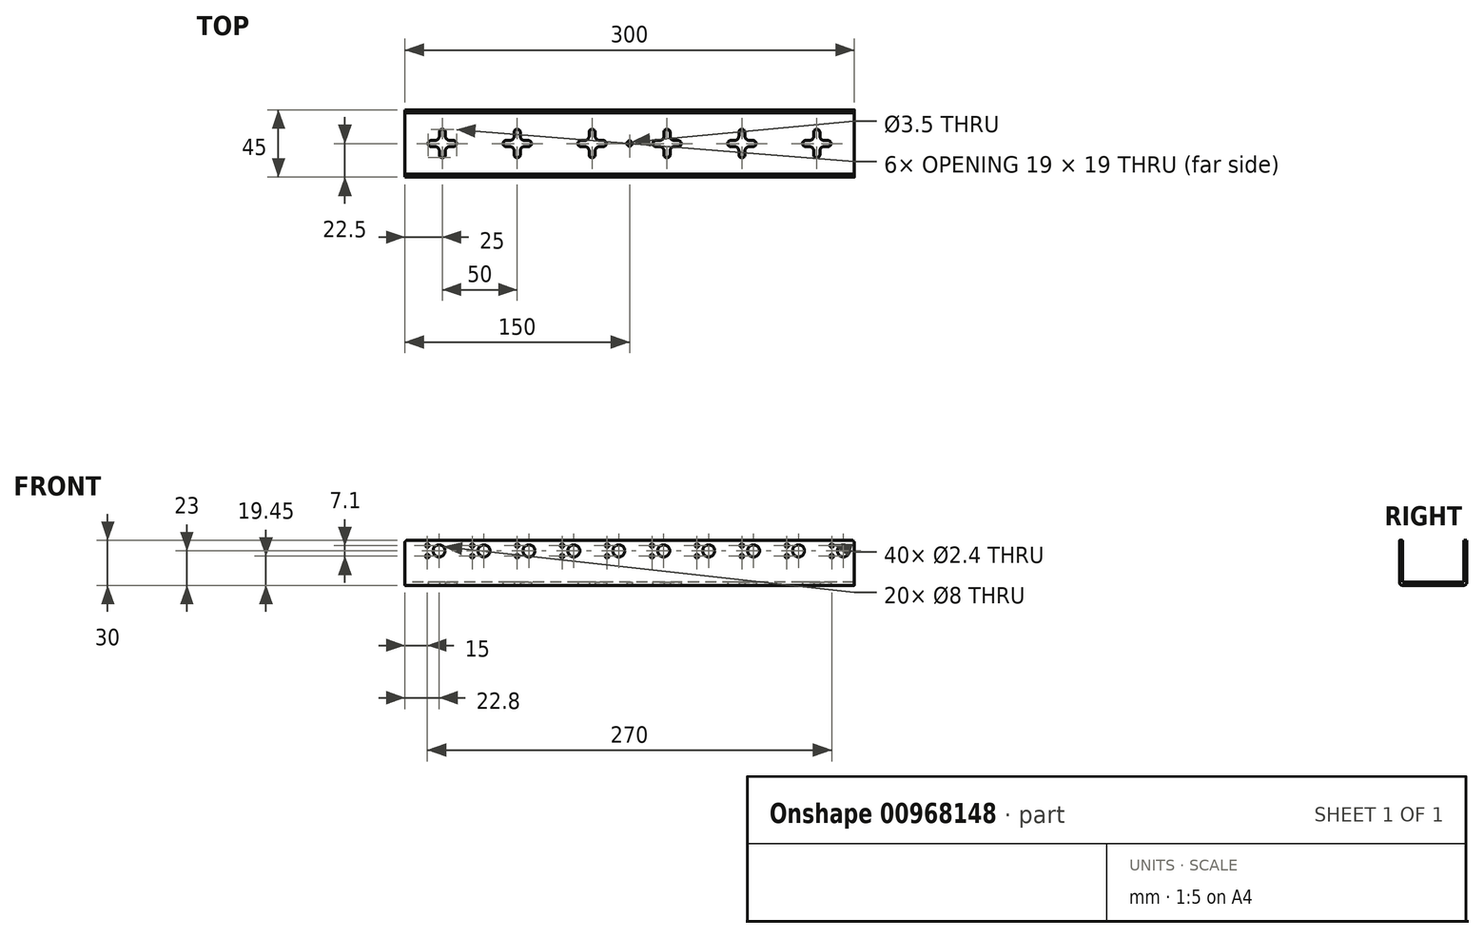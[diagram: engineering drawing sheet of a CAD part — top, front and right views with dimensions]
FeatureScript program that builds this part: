
annotation { "Feature Type Name" : "Feature", "Feature Type Description" : "" }
export const myFeature = defineFeature(function(context is Context, id is Id, definition is map)
    precondition{}
    {
        {
            var Q0;
            Q0=qCreatedBy(makeId("Right.planeOp"),FACE);
            var sketch = newSketch(context, id + "F0", { "sketchPlane" : qUnion([Q0])});
            skLineSegment(sketch, "E0", {"start": v(0, 30) * mm, "end": v(0, 0) * mm});
            skLineSegment(sketch, "E1", {"start": v(0, 0) * mm, "end": v(45, 0) * mm});
            skLineSegment(sketch, "E2", {"start": v(45, 0) * mm, "end": v(45, 30) * mm});
            skLineSegment(sketch, "E3.0", {"start": v(2, 30) * mm, "end": v(2, 0) * mm});
            skLineSegment(sketch, "E4.0", {"start": v(43, 0) * mm, "end": v(43, 30) * mm});
            skLineSegment(sketch, "E5.0", {"start": v(0, 2) * mm, "end": v(60, 2) * mm});
            skLineSegment(sketch, "E6", {"start": v(0, 30) * mm, "end": v(45, 30) * mm});
            skSolve(sketch);
        }
        {
            var Q0;
            {var subQ0=sQuery(id+"F0.wireOp",EDGE,"E6");var subQ1=sQuery(id+"F0.wireOp",EDGE,"E0");var subQ2=makeQuery(id+"F0.imprint","INTERSECT",VERTEX,{"derivedFrom":[subQ1,subQ0]});Q0=makeQuery(id+"F0.imprint","IMPRINT",FACE,{"disambiguationData":[TD([[makeQuery(id+"F0.imprint","IMPRINT",EDGE,{"disambiguationData":[TD([[subQ2,-1.0]])],"derivedFrom":subQ1}),1.0]])]});}
            var Q1;
            {var subQ0=sQuery(id+"F0.wireOp",EDGE,"E1");var subQ1=sQuery(id+"F0.wireOp",EDGE,"E0");var subQ2=makeQuery(id+"F0.imprint","INTERSECT",VERTEX,{"derivedFrom":[subQ1,subQ0]});Q1=makeQuery(id+"F0.imprint","IMPRINT",FACE,{"disambiguationData":[TD([[makeQuery(id+"F0.imprint","IMPRINT",EDGE,{"disambiguationData":[TD([[subQ2,1.0]])],"derivedFrom":subQ1}),1.0]])]});}
            var Q2;
            {var subQ0=sQuery(id+"F0.wireOp",EDGE,"E3.0");var subQ1=sQuery(id+"F0.wireOp",EDGE,"E1");var subQ2=makeQuery(id+"F0.imprint","INTERSECT",VERTEX,{"derivedFrom":[subQ1,subQ0]});Q2=makeQuery(id+"F0.imprint","IMPRINT",FACE,{"disambiguationData":[TD([[makeQuery(id+"F0.imprint","IMPRINT",EDGE,{"disambiguationData":[TD([[subQ2,-1.0]])],"derivedFrom":subQ1}),1.0]])]});}
            var Q3;
            {var subQ0=sQuery(id+"F0.wireOp",EDGE,"E2");var subQ1=sQuery(id+"F0.wireOp",EDGE,"E1");var subQ2=makeQuery(id+"F0.imprint","INTERSECT",VERTEX,{"derivedFrom":[subQ1,subQ0]});Q3=makeQuery(id+"F0.imprint","IMPRINT",FACE,{"disambiguationData":[TD([[makeQuery(id+"F0.imprint","IMPRINT",EDGE,{"disambiguationData":[TD([[subQ2,1.0]])],"derivedFrom":subQ1}),1.0]])]});}
            var Q4;
            {var subQ0=sQuery(id+"F0.wireOp",EDGE,"E6");var subQ1=sQuery(id+"F0.wireOp",EDGE,"E2");var subQ2=makeQuery(id+"F0.imprint","INTERSECT",VERTEX,{"derivedFrom":[subQ1,subQ0]});Q4=makeQuery(id+"F0.imprint","IMPRINT",FACE,{"disambiguationData":[TD([[makeQuery(id+"F0.imprint","IMPRINT",EDGE,{"disambiguationData":[TD([[subQ2,1.0]])],"derivedFrom":subQ1}),1.0]])]});}
            extrude(context, id + "F1", {"entities" : qUnion([Q0, Q1, Q2, Q3, Q4]), "endBound" : BoundingType.SYMMETRIC, "depth" : 300 * mm, "offsetDistance" : 25 * mm});
        }
        {
            var Q0;
            Q0=makeQuery(id+"F1.opExtrude","SWEPT_FACE",FACE,{"disambiguationData":[OSD([sQuery(id+"F0.wireOp",EDGE,"E0")])]});
            var sketch = newSketch(context, id + "F2", { "sketchPlane" : qUnion([Q0])});
            skCircle(sketch, "E7", {"center": v(-135, 26.55) * mm, "radius": 1.2 * mm});
            skCircle(sketch, "E8", {"center": v(-135, 19.45) * mm, "radius": 1.2 * mm});
            skCircle(sketch, "E9", {"center": v(-127.2, 23) * mm, "radius": 4 * mm});
            skCircle(sketch, "E10", {"center": v(-105, 26.55) * mm, "radius": 1.2 * mm});
            skCircle(sketch, "E11", {"center": v(-105, 19.45) * mm, "radius": 1.2 * mm});
            skCircle(sketch, "E12", {"center": v(-97.2, 23) * mm, "radius": 4 * mm});
            skCircle(sketch, "E13.1.0.0", {"center": v(-75, 19.45) * mm, "radius": 1.2 * mm});
            skCircle(sketch, "E13.1.0.1", {"center": v(-67.2, 23) * mm, "radius": 4 * mm});
            skCircle(sketch, "E13.1.0.2", {"center": v(-75, 26.55) * mm, "radius": 1.2 * mm});
            skCircle(sketch, "E13.2.0.0", {"center": v(-45, 19.45) * mm, "radius": 1.2 * mm});
            skCircle(sketch, "E13.2.0.1", {"center": v(-37.2, 23) * mm, "radius": 4 * mm});
            skCircle(sketch, "E13.2.0.2", {"center": v(-45, 26.55) * mm, "radius": 1.2 * mm});
            skCircle(sketch, "E13.3.0.0", {"center": v(-15, 19.45) * mm, "radius": 1.2 * mm});
            skCircle(sketch, "E13.3.0.1", {"center": v(-7.2, 23) * mm, "radius": 4 * mm});
            skCircle(sketch, "E13.3.0.2", {"center": v(-15, 26.55) * mm, "radius": 1.2 * mm});
            skCircle(sketch, "E13.4.0.0", {"center": v(15, 19.45) * mm, "radius": 1.2 * mm});
            skCircle(sketch, "E13.4.0.1", {"center": v(22.8, 23) * mm, "radius": 4 * mm});
            skCircle(sketch, "E13.4.0.2", {"center": v(15, 26.55) * mm, "radius": 1.2 * mm});
            skCircle(sketch, "E13.5.0.0", {"center": v(45, 19.45) * mm, "radius": 1.2 * mm});
            skCircle(sketch, "E13.5.0.1", {"center": v(52.8, 23) * mm, "radius": 4 * mm});
            skCircle(sketch, "E13.5.0.2", {"center": v(45, 26.55) * mm, "radius": 1.2 * mm});
            skCircle(sketch, "E13.6.0.0", {"center": v(75, 19.45) * mm, "radius": 1.2 * mm});
            skCircle(sketch, "E13.6.0.1", {"center": v(82.8, 23) * mm, "radius": 4 * mm});
            skCircle(sketch, "E13.6.0.2", {"center": v(75, 26.55) * mm, "radius": 1.2 * mm});
            skCircle(sketch, "E13.7.0.0", {"center": v(105, 19.45) * mm, "radius": 1.2 * mm});
            skCircle(sketch, "E13.7.0.1", {"center": v(112.8, 23) * mm, "radius": 4 * mm});
            skCircle(sketch, "E13.7.0.2", {"center": v(105, 26.55) * mm, "radius": 1.2 * mm});
            skCircle(sketch, "E13.8.0.0", {"center": v(135, 19.45) * mm, "radius": 1.2 * mm});
            skCircle(sketch, "E13.8.0.1", {"center": v(142.8, 23) * mm, "radius": 4 * mm});
            skCircle(sketch, "E13.8.0.2", {"center": v(135, 26.55) * mm, "radius": 1.2 * mm});
            skLineSegment(sketch, "E13.direction1", {"start": v(-105, 19.45) * mm, "end": v(-75, 19.45) * mm, "construction": true});
            skSolve(sketch);
        }
        {
            var Q0;
            Q0=makeQuery(id+"F2.imprint","IMPRINT",FACE,{"disambiguationData":[TD([[makeQuery(id+"F2.imprint","IMPRINT",EDGE,{"derivedFrom":sQuery(id+"F2.wireOp",EDGE,"E7")}),1.0]])]});
            var Q1;
            Q1=makeQuery(id+"F2.imprint","IMPRINT",FACE,{"disambiguationData":[TD([[makeQuery(id+"F2.imprint","IMPRINT",EDGE,{"derivedFrom":sQuery(id+"F2.wireOp",EDGE,"E8")}),1.0]])]});
            var Q2;
            Q2=makeQuery(id+"F2.imprint","IMPRINT",FACE,{"disambiguationData":[TD([[makeQuery(id+"F2.imprint","IMPRINT",EDGE,{"derivedFrom":sQuery(id+"F2.wireOp",EDGE,"E10")}),1.0]])]});
            var Q3;
            Q3=makeQuery(id+"F2.imprint","IMPRINT",FACE,{"disambiguationData":[TD([[makeQuery(id+"F2.imprint","IMPRINT",EDGE,{"derivedFrom":sQuery(id+"F2.wireOp",EDGE,"E11")}),1.0]])]});
            var Q4;
            Q4=makeQuery(id+"F2.imprint","IMPRINT",FACE,{"disambiguationData":[TD([[makeQuery(id+"F2.imprint","IMPRINT",EDGE,{"derivedFrom":sQuery(id+"F2.wireOp",EDGE,"E12")}),1.0]])]});
            var Q5;
            Q5=makeQuery(id+"F2.imprint","IMPRINT",FACE,{"disambiguationData":[TD([[makeQuery(id+"F2.imprint","IMPRINT",EDGE,{"derivedFrom":sQuery(id+"F2.wireOp",EDGE,"E13.1.0.1")}),1.0]])]});
            var Q6;
            Q6=makeQuery(id+"F2.imprint","IMPRINT",FACE,{"disambiguationData":[TD([[makeQuery(id+"F2.imprint","IMPRINT",EDGE,{"derivedFrom":sQuery(id+"F2.wireOp",EDGE,"E13.1.0.2")}),1.0]])]});
            var Q7;
            Q7=makeQuery(id+"F2.imprint","IMPRINT",FACE,{"disambiguationData":[TD([[makeQuery(id+"F2.imprint","IMPRINT",EDGE,{"derivedFrom":sQuery(id+"F2.wireOp",EDGE,"E13.1.0.0")}),1.0]])]});
            var Q8;
            Q8=makeQuery(id+"F2.imprint","IMPRINT",FACE,{"disambiguationData":[TD([[makeQuery(id+"F2.imprint","IMPRINT",EDGE,{"derivedFrom":sQuery(id+"F2.wireOp",EDGE,"E13.2.0.0")}),1.0]])]});
            var Q9;
            Q9=makeQuery(id+"F2.imprint","IMPRINT",FACE,{"disambiguationData":[TD([[makeQuery(id+"F2.imprint","IMPRINT",EDGE,{"derivedFrom":sQuery(id+"F2.wireOp",EDGE,"E13.3.0.1")}),1.0]])]});
            var Q10;
            Q10=makeQuery(id+"F2.imprint","IMPRINT",FACE,{"disambiguationData":[TD([[makeQuery(id+"F2.imprint","IMPRINT",EDGE,{"derivedFrom":sQuery(id+"F2.wireOp",EDGE,"E13.3.0.2")}),1.0]])]});
            var Q11;
            Q11=makeQuery(id+"F2.imprint","IMPRINT",FACE,{"disambiguationData":[TD([[makeQuery(id+"F2.imprint","IMPRINT",EDGE,{"derivedFrom":sQuery(id+"F2.wireOp",EDGE,"E9")}),1.0]])]});
            var Q12;
            Q12=makeQuery(id+"F2.imprint","IMPRINT",FACE,{"disambiguationData":[TD([[makeQuery(id+"F2.imprint","IMPRINT",EDGE,{"derivedFrom":sQuery(id+"F2.wireOp",EDGE,"E13.2.0.1")}),1.0]])]});
            var Q13;
            Q13=makeQuery(id+"F2.imprint","IMPRINT",FACE,{"disambiguationData":[TD([[makeQuery(id+"F2.imprint","IMPRINT",EDGE,{"derivedFrom":sQuery(id+"F2.wireOp",EDGE,"E13.2.0.2")}),1.0]])]});
            var Q14;
            Q14=makeQuery(id+"F2.imprint","IMPRINT",FACE,{"disambiguationData":[TD([[makeQuery(id+"F2.imprint","IMPRINT",EDGE,{"derivedFrom":sQuery(id+"F2.wireOp",EDGE,"E13.3.0.0")}),1.0]])]});
            var Q15;
            Q15=makeQuery(id+"F2.imprint","IMPRINT",FACE,{"disambiguationData":[TD([[makeQuery(id+"F2.imprint","IMPRINT",EDGE,{"derivedFrom":sQuery(id+"F2.wireOp",EDGE,"E13.4.0.1")}),1.0]])]});
            var Q16;
            Q16=makeQuery(id+"F2.imprint","IMPRINT",FACE,{"disambiguationData":[TD([[makeQuery(id+"F2.imprint","IMPRINT",EDGE,{"derivedFrom":sQuery(id+"F2.wireOp",EDGE,"E13.4.0.2")}),1.0]])]});
            var Q17;
            Q17=makeQuery(id+"F2.imprint","IMPRINT",FACE,{"disambiguationData":[TD([[makeQuery(id+"F2.imprint","IMPRINT",EDGE,{"derivedFrom":sQuery(id+"F2.wireOp",EDGE,"E13.4.0.0")}),1.0]])]});
            var Q18;
            Q18=makeQuery(id+"F2.imprint","IMPRINT",FACE,{"disambiguationData":[TD([[makeQuery(id+"F2.imprint","IMPRINT",EDGE,{"derivedFrom":sQuery(id+"F2.wireOp",EDGE,"E13.5.0.1")}),1.0]])]});
            var Q19;
            Q19=makeQuery(id+"F2.imprint","IMPRINT",FACE,{"disambiguationData":[TD([[makeQuery(id+"F2.imprint","IMPRINT",EDGE,{"derivedFrom":sQuery(id+"F2.wireOp",EDGE,"E13.5.0.2")}),1.0]])]});
            var Q20;
            Q20=makeQuery(id+"F2.imprint","IMPRINT",FACE,{"disambiguationData":[TD([[makeQuery(id+"F2.imprint","IMPRINT",EDGE,{"derivedFrom":sQuery(id+"F2.wireOp",EDGE,"E13.5.0.0")}),1.0]])]});
            var Q21;
            Q21=makeQuery(id+"F2.imprint","IMPRINT",FACE,{"disambiguationData":[TD([[makeQuery(id+"F2.imprint","IMPRINT",EDGE,{"derivedFrom":sQuery(id+"F2.wireOp",EDGE,"E13.6.0.1")}),1.0]])]});
            var Q22;
            Q22=makeQuery(id+"F2.imprint","IMPRINT",FACE,{"disambiguationData":[TD([[makeQuery(id+"F2.imprint","IMPRINT",EDGE,{"derivedFrom":sQuery(id+"F2.wireOp",EDGE,"E13.6.0.0")}),1.0]])]});
            var Q23;
            Q23=makeQuery(id+"F2.imprint","IMPRINT",FACE,{"disambiguationData":[TD([[makeQuery(id+"F2.imprint","IMPRINT",EDGE,{"derivedFrom":sQuery(id+"F2.wireOp",EDGE,"E13.6.0.2")}),1.0]])]});
            var Q24;
            Q24=makeQuery(id+"F2.imprint","IMPRINT",FACE,{"disambiguationData":[TD([[makeQuery(id+"F2.imprint","IMPRINT",EDGE,{"derivedFrom":sQuery(id+"F2.wireOp",EDGE,"E13.7.0.1")}),1.0]])]});
            var Q25;
            Q25=makeQuery(id+"F2.imprint","IMPRINT",FACE,{"disambiguationData":[TD([[makeQuery(id+"F2.imprint","IMPRINT",EDGE,{"derivedFrom":sQuery(id+"F2.wireOp",EDGE,"E13.7.0.2")}),1.0]])]});
            var Q26;
            Q26=makeQuery(id+"F2.imprint","IMPRINT",FACE,{"disambiguationData":[TD([[makeQuery(id+"F2.imprint","IMPRINT",EDGE,{"derivedFrom":sQuery(id+"F2.wireOp",EDGE,"E13.7.0.0")}),1.0]])]});
            var Q27;
            Q27=makeQuery(id+"F2.imprint","IMPRINT",FACE,{"disambiguationData":[TD([[makeQuery(id+"F2.imprint","IMPRINT",EDGE,{"derivedFrom":sQuery(id+"F2.wireOp",EDGE,"E13.8.0.1")}),1.0]])]});
            var Q28;
            Q28=makeQuery(id+"F2.imprint","IMPRINT",FACE,{"disambiguationData":[TD([[makeQuery(id+"F2.imprint","IMPRINT",EDGE,{"derivedFrom":sQuery(id+"F2.wireOp",EDGE,"E13.8.0.2")}),1.0]])]});
            var Q29;
            Q29=makeQuery(id+"F2.imprint","IMPRINT",FACE,{"disambiguationData":[TD([[makeQuery(id+"F2.imprint","IMPRINT",EDGE,{"derivedFrom":sQuery(id+"F2.wireOp",EDGE,"E13.8.0.0")}),1.0]])]});
            extrude(context, id + "F3", {"entities" : qUnion([Q0, Q1, Q2, Q3, Q4, Q5, Q6, Q7, Q8, Q9, Q10, Q11, Q12, Q13, Q14, Q15, Q16, Q17, Q18, Q19, Q20, Q21, Q22, Q23, Q24, Q25, Q26, Q27, Q28, Q29]), "operationType" : NewBodyOperationType.REMOVE, "endBound" : BoundingType.THROUGH_ALL, "oppositeDirection" : true, "depth" : 25 * mm, "offsetDistance" : 25 * mm});
        }
        {
            var Q0;
            {var subQ0=sQuery(id+"F0.wireOp",EDGE,"E6");Q0=makeQuery(id+"F1.opExtrude","CAP_EDGE",EDGE,{"disambiguationData":[OSD([subQ0]),TDD([makeQuery(id+"F0.imprint","IMPRINT",EDGE,{"disambiguationData":[TD([[makeQuery(id+"F0.imprint","INTERSECT",VERTEX,{"derivedFrom":[sQuery(id+"F0.wireOp",EDGE,"E2"),subQ0]}),1.0]])],"derivedFrom":subQ0})])],"isStart":true});}
            var Q1;
            {var subQ0=sQuery(id+"F0.wireOp",EDGE,"E6");Q1=makeQuery(id+"F1.opExtrude","CAP_EDGE",EDGE,{"disambiguationData":[OSD([subQ0]),TDD([makeQuery(id+"F0.imprint","IMPRINT",EDGE,{"disambiguationData":[TD([[makeQuery(id+"F0.imprint","INTERSECT",VERTEX,{"derivedFrom":[sQuery(id+"F0.wireOp",EDGE,"E2"),subQ0]}),1.0]])],"derivedFrom":subQ0})])],"isStart":false});}
            var Q2;
            {var subQ0=sQuery(id+"F0.wireOp",EDGE,"E6");Q2=makeQuery(id+"F1.opExtrude","CAP_EDGE",EDGE,{"disambiguationData":[OSD([subQ0]),TDD([makeQuery(id+"F0.imprint","IMPRINT",EDGE,{"disambiguationData":[TD([[makeQuery(id+"F0.imprint","INTERSECT",VERTEX,{"derivedFrom":[sQuery(id+"F0.wireOp",EDGE,"E0"),subQ0]}),-1.0]])],"derivedFrom":subQ0})])],"isStart":false});}
            var Q3;
            {var subQ0=sQuery(id+"F0.wireOp",EDGE,"E6");Q3=makeQuery(id+"F1.opExtrude","CAP_EDGE",EDGE,{"disambiguationData":[OSD([subQ0]),TDD([makeQuery(id+"F0.imprint","IMPRINT",EDGE,{"disambiguationData":[TD([[makeQuery(id+"F0.imprint","INTERSECT",VERTEX,{"derivedFrom":[sQuery(id+"F0.wireOp",EDGE,"E0"),subQ0]}),-1.0]])],"derivedFrom":subQ0})])],"isStart":true});}
            fillet(context, id + "F4", {"entities" : qUnion([Q0, Q1, Q2, Q3]), "radius" : 1.5 * mm, "tangentPropagation" : true, "allowEdgeOverflow" : false});
        }
        {
            var Q0;
            Q0=makeQuery(id+"F1.opExtrude","SWEPT_EDGE",EDGE,{"disambiguationData":[OSD([sQuery(id+"F0.wireOp",EDGE,"E0"),sQuery(id+"F0.wireOp",EDGE,"E1")])]});
            var Q1;
            Q1=makeQuery(id+"F1.opExtrude","SWEPT_EDGE",EDGE,{"disambiguationData":[OSD([sQuery(id+"F0.wireOp",EDGE,"E1"),sQuery(id+"F0.wireOp",EDGE,"E2")])]});
            fillet(context, id + "F5", {"entities" : qUnion([Q0, Q1]), "radius" : 2 * mm, "tangentPropagation" : true, "allowEdgeOverflow" : false});
        }
        {
            var Q0;
            Q0=makeQuery(id+"F1.opExtrude","SWEPT_FACE",FACE,{"disambiguationData":[OSD([sQuery(id+"F0.wireOp",EDGE,"E1")])]});
            var sketch = newSketch(context, id + "F6", { "sketchPlane" : qUnion([Q0])});
            skCircle(sketch, "E14", {"center": v(0, -22.5) * mm, "radius": 1.75 * mm});
            skLineSegment(sketch, "E15", {"start": v(-25, -30) * mm, "end": v(-25, -15) * mm});
            skLineSegment(sketch, "E16", {"start": v(-17.5, -22.5) * mm, "end": v(-32.5, -22.5) * mm});
            skArc(sketch, "E17.0.startCap", {"start": v(-17.5, -20.5) * mm, "mid": v(-15.5, -22.5) * mm, "end": v(-17.5, -24.5) * mm});
            skArc(sketch, "E17.0.endCap", {"start": v(-32.5, -24.5) * mm, "mid": v(-34.5, -22.5) * mm, "end": v(-32.5, -20.5) * mm});
            skLineSegment(sketch, "E17.0.left", {"start": v(-17.5, -24.5) * mm, "end": v(-32.5, -24.5) * mm});
            skLineSegment(sketch, "E17.0.right", {"start": v(-17.5, -20.5) * mm, "end": v(-32.5, -20.5) * mm});
            skArc(sketch, "E17.1.startCap", {"start": v(-23, -30) * mm, "mid": v(-25, -32) * mm, "end": v(-27, -30) * mm});
            skArc(sketch, "E17.1.endCap", {"start": v(-27, -15) * mm, "mid": v(-25, -13) * mm, "end": v(-23, -15) * mm});
            skLineSegment(sketch, "E17.1.left", {"start": v(-27, -30) * mm, "end": v(-27, -15) * mm});
            skLineSegment(sketch, "E17.1.right", {"start": v(-23, -30) * mm, "end": v(-23, -15) * mm});
            skArc(sketch, "E18.1.0.0", {"start": v(-82.5, -24.5) * mm, "mid": v(-84.5, -22.5) * mm, "end": v(-82.5, -20.5) * mm});
            skArc(sketch, "E18.1.0.1", {"start": v(-77, -15) * mm, "mid": v(-75, -13) * mm, "end": v(-73, -15) * mm});
            skLineSegment(sketch, "E18.1.0.2", {"start": v(-73, -30) * mm, "end": v(-73, -15) * mm});
            skLineSegment(sketch, "E18.1.0.3", {"start": v(-67.5, -24.5) * mm, "end": v(-82.5, -24.5) * mm});
            skArc(sketch, "E18.1.0.4", {"start": v(-67.5, -20.5) * mm, "mid": v(-65.5, -22.5) * mm, "end": v(-67.5, -24.5) * mm});
            skLineSegment(sketch, "E18.1.0.5", {"start": v(-75, -30) * mm, "end": v(-75, -15) * mm});
            skArc(sketch, "E18.1.0.6", {"start": v(-73, -30) * mm, "mid": v(-75, -32) * mm, "end": v(-77, -30) * mm});
            skLineSegment(sketch, "E18.1.0.7", {"start": v(-67.5, -22.5) * mm, "end": v(-82.5, -22.5) * mm});
            skLineSegment(sketch, "E18.1.0.8", {"start": v(-77, -30) * mm, "end": v(-77, -15) * mm});
            skLineSegment(sketch, "E18.1.0.9", {"start": v(-67.5, -20.5) * mm, "end": v(-82.5, -20.5) * mm});
            skArc(sketch, "E18.2.0.0", {"start": v(-132.5, -24.5) * mm, "mid": v(-134.5, -22.5) * mm, "end": v(-132.5, -20.5) * mm});
            skArc(sketch, "E18.2.0.1", {"start": v(-127, -15) * mm, "mid": v(-125, -13) * mm, "end": v(-123, -15) * mm});
            skLineSegment(sketch, "E18.2.0.2", {"start": v(-123, -30) * mm, "end": v(-123, -15) * mm});
            skLineSegment(sketch, "E18.2.0.3", {"start": v(-117.5, -24.5) * mm, "end": v(-132.5, -24.5) * mm});
            skArc(sketch, "E18.2.0.4", {"start": v(-117.5, -20.5) * mm, "mid": v(-115.5, -22.5) * mm, "end": v(-117.5, -24.5) * mm});
            skLineSegment(sketch, "E18.2.0.5", {"start": v(-125, -30) * mm, "end": v(-125, -15) * mm});
            skArc(sketch, "E18.2.0.6", {"start": v(-123, -30) * mm, "mid": v(-125, -32) * mm, "end": v(-127, -30) * mm});
            skLineSegment(sketch, "E18.2.0.7", {"start": v(-117.5, -22.5) * mm, "end": v(-132.5, -22.5) * mm});
            skLineSegment(sketch, "E18.2.0.8", {"start": v(-127, -30) * mm, "end": v(-127, -15) * mm});
            skLineSegment(sketch, "E18.2.0.9", {"start": v(-117.5, -20.5) * mm, "end": v(-132.5, -20.5) * mm});
            skLineSegment(sketch, "E18.direction1", {"start": v(-27, -30) * mm, "end": v(-77, -30) * mm, "construction": true});
            skLineSegment(sketch, "E19.1.0.0", {"start": v(25, -30) * mm, "end": v(25, -15) * mm});
            skArc(sketch, "E19.1.0.1", {"start": v(32.5, -20.5) * mm, "mid": v(34.5, -22.5) * mm, "end": v(32.5, -24.5) * mm});
            skArc(sketch, "E19.1.0.2", {"start": v(17.5, -24.5) * mm, "mid": v(15.5, -22.5) * mm, "end": v(17.5, -20.5) * mm});
            skLineSegment(sketch, "E19.1.0.3", {"start": v(27, -30) * mm, "end": v(27, -15) * mm});
            skLineSegment(sketch, "E19.1.0.4", {"start": v(32.5, -24.5) * mm, "end": v(17.5, -24.5) * mm});
            skLineSegment(sketch, "E19.1.0.5", {"start": v(32.5, -22.5) * mm, "end": v(17.5, -22.5) * mm});
            skArc(sketch, "E19.1.0.6", {"start": v(27, -30) * mm, "mid": v(25, -32) * mm, "end": v(23, -30) * mm});
            skLineSegment(sketch, "E19.1.0.7", {"start": v(23, -30) * mm, "end": v(23, -15) * mm});
            skLineSegment(sketch, "E19.1.0.8", {"start": v(32.5, -20.5) * mm, "end": v(17.5, -20.5) * mm});
            skArc(sketch, "E19.1.0.9", {"start": v(23, -15) * mm, "mid": v(25, -13) * mm, "end": v(27, -15) * mm});
            skLineSegment(sketch, "E19.2.0.0", {"start": v(75, -30) * mm, "end": v(75, -15) * mm});
            skArc(sketch, "E19.2.0.1", {"start": v(82.5, -20.5) * mm, "mid": v(84.5, -22.5) * mm, "end": v(82.5, -24.5) * mm});
            skArc(sketch, "E19.2.0.2", {"start": v(67.5, -24.5) * mm, "mid": v(65.5, -22.5) * mm, "end": v(67.5, -20.5) * mm});
            skLineSegment(sketch, "E19.2.0.3", {"start": v(77, -30) * mm, "end": v(77, -15) * mm});
            skLineSegment(sketch, "E19.2.0.4", {"start": v(82.5, -24.5) * mm, "end": v(67.5, -24.5) * mm});
            skLineSegment(sketch, "E19.2.0.5", {"start": v(82.5, -22.5) * mm, "end": v(67.5, -22.5) * mm});
            skArc(sketch, "E19.2.0.6", {"start": v(77, -30) * mm, "mid": v(75, -32) * mm, "end": v(73, -30) * mm});
            skLineSegment(sketch, "E19.2.0.7", {"start": v(73, -30) * mm, "end": v(73, -15) * mm});
            skLineSegment(sketch, "E19.2.0.8", {"start": v(82.5, -20.5) * mm, "end": v(67.5, -20.5) * mm});
            skArc(sketch, "E19.2.0.9", {"start": v(73, -15) * mm, "mid": v(75, -13) * mm, "end": v(77, -15) * mm});
            skLineSegment(sketch, "E19.3.0.0", {"start": v(125, -30) * mm, "end": v(125, -15) * mm});
            skArc(sketch, "E19.3.0.1", {"start": v(132.5, -20.5) * mm, "mid": v(134.5, -22.5) * mm, "end": v(132.5, -24.5) * mm});
            skArc(sketch, "E19.3.0.2", {"start": v(117.5, -24.5) * mm, "mid": v(115.5, -22.5) * mm, "end": v(117.5, -20.5) * mm});
            skLineSegment(sketch, "E19.3.0.3", {"start": v(127, -30) * mm, "end": v(127, -15) * mm});
            skLineSegment(sketch, "E19.3.0.4", {"start": v(132.5, -24.5) * mm, "end": v(117.5, -24.5) * mm});
            skLineSegment(sketch, "E19.3.0.5", {"start": v(132.5, -22.5) * mm, "end": v(117.5, -22.5) * mm});
            skArc(sketch, "E19.3.0.6", {"start": v(127, -30) * mm, "mid": v(125, -32) * mm, "end": v(123, -30) * mm});
            skLineSegment(sketch, "E19.3.0.7", {"start": v(123, -30) * mm, "end": v(123, -15) * mm});
            skLineSegment(sketch, "E19.3.0.8", {"start": v(132.5, -20.5) * mm, "end": v(117.5, -20.5) * mm});
            skArc(sketch, "E19.3.0.9", {"start": v(123, -15) * mm, "mid": v(125, -13) * mm, "end": v(127, -15) * mm});
            skLineSegment(sketch, "E19.direction1", {"start": v(-27, -30) * mm, "end": v(23, -30) * mm, "construction": true});
            skSolve(sketch);
        }
        {
            var Q0;
            Q0 = qSketchRegion(id + "F6", true);
            extrude(context, id + "F7", {"entities" : qUnion([Q0]), "operationType" : NewBodyOperationType.REMOVE, "oppositeDirection" : true, "depth" : 2 * mm, "offsetDistance" : 25 * mm});
        }
        {
            var Q0;
            Q0=makeQuery(id+"F7.boolean.opBoolean","COPY",EDGE,{"derivedFrom":makeQuery(id+"F7.opExtrude","SWEPT_EDGE",EDGE,{"disambiguationData":[OSD([sQuery(id+"F6.wireOp",EDGE,"E19.3.0.7"),sQuery(id+"F6.wireOp",EDGE,"E19.3.0.8")])]})});
            var Q1;
            Q1=makeQuery(id+"F7.boolean.opBoolean","COPY",EDGE,{"derivedFrom":makeQuery(id+"F7.opExtrude","SWEPT_EDGE",EDGE,{"disambiguationData":[OSD([sQuery(id+"F6.wireOp",EDGE,"E19.3.0.3"),sQuery(id+"F6.wireOp",EDGE,"E19.3.0.8")])]})});
            var Q2;
            Q2=makeQuery(id+"F7.boolean.opBoolean","COPY",EDGE,{"derivedFrom":makeQuery(id+"F7.opExtrude","SWEPT_EDGE",EDGE,{"disambiguationData":[OSD([sQuery(id+"F6.wireOp",EDGE,"E19.2.0.3"),sQuery(id+"F6.wireOp",EDGE,"E19.2.0.8")])]})});
            var Q3;
            Q3=makeQuery(id+"F7.boolean.opBoolean","COPY",EDGE,{"derivedFrom":makeQuery(id+"F7.opExtrude","SWEPT_EDGE",EDGE,{"disambiguationData":[OSD([sQuery(id+"F6.wireOp",EDGE,"E19.1.0.3"),sQuery(id+"F6.wireOp",EDGE,"E19.1.0.8")])]})});
            var Q4;
            Q4=makeQuery(id+"F7.boolean.opBoolean","COPY",EDGE,{"derivedFrom":makeQuery(id+"F7.opExtrude","SWEPT_EDGE",EDGE,{"disambiguationData":[OSD([sQuery(id+"F6.wireOp",EDGE,"E19.1.0.7"),sQuery(id+"F6.wireOp",EDGE,"E19.1.0.8")])]})});
            var Q5;
            Q5=makeQuery(id+"F7.boolean.opBoolean","COPY",EDGE,{"derivedFrom":makeQuery(id+"F7.opExtrude","SWEPT_EDGE",EDGE,{"disambiguationData":[OSD([sQuery(id+"F6.wireOp",EDGE,"E17.0.right"),sQuery(id+"F6.wireOp",EDGE,"E17.1.right")])]})});
            var Q6;
            Q6=makeQuery(id+"F7.boolean.opBoolean","COPY",EDGE,{"derivedFrom":makeQuery(id+"F7.opExtrude","SWEPT_EDGE",EDGE,{"disambiguationData":[OSD([sQuery(id+"F6.wireOp",EDGE,"E17.0.right"),sQuery(id+"F6.wireOp",EDGE,"E17.1.left")])]})});
            var Q7;
            Q7=makeQuery(id+"F7.boolean.opBoolean","COPY",EDGE,{"derivedFrom":makeQuery(id+"F7.opExtrude","SWEPT_EDGE",EDGE,{"disambiguationData":[OSD([sQuery(id+"F6.wireOp",EDGE,"E18.1.0.2"),sQuery(id+"F6.wireOp",EDGE,"E18.1.0.9")])]})});
            var Q8;
            Q8=makeQuery(id+"F7.boolean.opBoolean","COPY",EDGE,{"derivedFrom":makeQuery(id+"F7.opExtrude","SWEPT_EDGE",EDGE,{"disambiguationData":[OSD([sQuery(id+"F6.wireOp",EDGE,"E18.1.0.8"),sQuery(id+"F6.wireOp",EDGE,"E18.1.0.9")])]})});
            var Q9;
            Q9=makeQuery(id+"F7.boolean.opBoolean","COPY",EDGE,{"derivedFrom":makeQuery(id+"F7.opExtrude","SWEPT_EDGE",EDGE,{"disambiguationData":[OSD([sQuery(id+"F6.wireOp",EDGE,"E18.2.0.2"),sQuery(id+"F6.wireOp",EDGE,"E18.2.0.9")])]})});
            var Q10;
            Q10=makeQuery(id+"F7.boolean.opBoolean","COPY",EDGE,{"derivedFrom":makeQuery(id+"F7.opExtrude","SWEPT_EDGE",EDGE,{"disambiguationData":[OSD([sQuery(id+"F6.wireOp",EDGE,"E18.2.0.8"),sQuery(id+"F6.wireOp",EDGE,"E18.2.0.9")])]})});
            var Q11;
            Q11=makeQuery(id+"F7.boolean.opBoolean","COPY",EDGE,{"derivedFrom":makeQuery(id+"F7.opExtrude","SWEPT_EDGE",EDGE,{"disambiguationData":[OSD([sQuery(id+"F6.wireOp",EDGE,"E18.2.0.3"),sQuery(id+"F6.wireOp",EDGE,"E18.2.0.8")])]})});
            var Q12;
            Q12=makeQuery(id+"F7.boolean.opBoolean","COPY",EDGE,{"derivedFrom":makeQuery(id+"F7.opExtrude","SWEPT_EDGE",EDGE,{"disambiguationData":[OSD([sQuery(id+"F6.wireOp",EDGE,"E18.2.0.2"),sQuery(id+"F6.wireOp",EDGE,"E18.2.0.3")])]})});
            var Q13;
            Q13=makeQuery(id+"F7.boolean.opBoolean","COPY",EDGE,{"derivedFrom":makeQuery(id+"F7.opExtrude","SWEPT_EDGE",EDGE,{"disambiguationData":[OSD([sQuery(id+"F6.wireOp",EDGE,"E18.1.0.3"),sQuery(id+"F6.wireOp",EDGE,"E18.1.0.8")])]})});
            var Q14;
            Q14=makeQuery(id+"F7.boolean.opBoolean","COPY",EDGE,{"derivedFrom":makeQuery(id+"F7.opExtrude","SWEPT_EDGE",EDGE,{"disambiguationData":[OSD([sQuery(id+"F6.wireOp",EDGE,"E18.1.0.2"),sQuery(id+"F6.wireOp",EDGE,"E18.1.0.3")])]})});
            var Q15;
            Q15=makeQuery(id+"F7.boolean.opBoolean","COPY",EDGE,{"derivedFrom":makeQuery(id+"F7.opExtrude","SWEPT_EDGE",EDGE,{"disambiguationData":[OSD([sQuery(id+"F6.wireOp",EDGE,"E17.0.left"),sQuery(id+"F6.wireOp",EDGE,"E17.1.left")])]})});
            var Q16;
            Q16=makeQuery(id+"F7.boolean.opBoolean","COPY",EDGE,{"derivedFrom":makeQuery(id+"F7.opExtrude","SWEPT_EDGE",EDGE,{"disambiguationData":[OSD([sQuery(id+"F6.wireOp",EDGE,"E17.0.left"),sQuery(id+"F6.wireOp",EDGE,"E17.1.right")])]})});
            var Q17;
            Q17=makeQuery(id+"F7.boolean.opBoolean","COPY",EDGE,{"derivedFrom":makeQuery(id+"F7.opExtrude","SWEPT_EDGE",EDGE,{"disambiguationData":[OSD([sQuery(id+"F6.wireOp",EDGE,"E19.1.0.3"),sQuery(id+"F6.wireOp",EDGE,"E19.1.0.4")])]})});
            var Q18;
            Q18=makeQuery(id+"F7.boolean.opBoolean","COPY",EDGE,{"derivedFrom":makeQuery(id+"F7.opExtrude","SWEPT_EDGE",EDGE,{"disambiguationData":[OSD([sQuery(id+"F6.wireOp",EDGE,"E19.1.0.4"),sQuery(id+"F6.wireOp",EDGE,"E19.1.0.7")])]})});
            var Q19;
            Q19=makeQuery(id+"F7.boolean.opBoolean","COPY",EDGE,{"derivedFrom":makeQuery(id+"F7.opExtrude","SWEPT_EDGE",EDGE,{"disambiguationData":[OSD([sQuery(id+"F6.wireOp",EDGE,"E19.2.0.3"),sQuery(id+"F6.wireOp",EDGE,"E19.2.0.4")])]})});
            var Q20;
            Q20=makeQuery(id+"F7.boolean.opBoolean","COPY",EDGE,{"derivedFrom":makeQuery(id+"F7.opExtrude","SWEPT_EDGE",EDGE,{"disambiguationData":[OSD([sQuery(id+"F6.wireOp",EDGE,"E19.2.0.4"),sQuery(id+"F6.wireOp",EDGE,"E19.2.0.7")])]})});
            var Q21;
            Q21=makeQuery(id+"F7.boolean.opBoolean","COPY",EDGE,{"derivedFrom":makeQuery(id+"F7.opExtrude","SWEPT_EDGE",EDGE,{"disambiguationData":[OSD([sQuery(id+"F6.wireOp",EDGE,"E19.3.0.3"),sQuery(id+"F6.wireOp",EDGE,"E19.3.0.4")])]})});
            var Q22;
            Q22=makeQuery(id+"F7.boolean.opBoolean","COPY",EDGE,{"derivedFrom":makeQuery(id+"F7.opExtrude","SWEPT_EDGE",EDGE,{"disambiguationData":[OSD([sQuery(id+"F6.wireOp",EDGE,"E19.3.0.4"),sQuery(id+"F6.wireOp",EDGE,"E19.3.0.7")])]})});
            var Q23;
            Q23=makeQuery(id+"F7.boolean.opBoolean","COPY",EDGE,{"derivedFrom":makeQuery(id+"F7.opExtrude","SWEPT_EDGE",EDGE,{"disambiguationData":[OSD([sQuery(id+"F6.wireOp",EDGE,"E19.2.0.7"),sQuery(id+"F6.wireOp",EDGE,"E19.2.0.8")])]})});
            fillet(context, id + "F8", {"entities" : qUnion([Q0, Q1, Q2, Q3, Q4, Q5, Q6, Q7, Q8, Q9, Q10, Q11, Q12, Q13, Q14, Q15, Q16, Q17, Q18, Q19, Q20, Q21, Q22, Q23]), "radius" : 3 * mm, "tangentPropagation" : true, "allowEdgeOverflow" : false});
        }
    });
